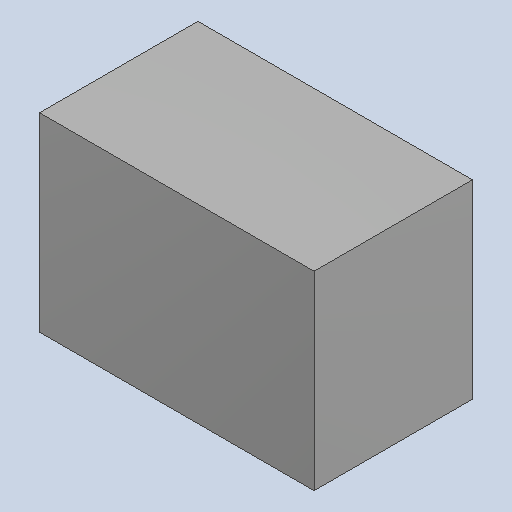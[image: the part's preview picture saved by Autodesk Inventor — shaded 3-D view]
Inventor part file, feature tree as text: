
AUTODESK INVENTOR PART (.ipt)
format: ipt  version: 2023.4 (Build 274418000, 418)  size: 82,432 bytes
history: native  units: mm
features: extrude x1
ambient origin geometry x8: Origin, YZ Plane, XZ Plane, XY Plane, X Axis, Y Axis, Z Axis, Center Point
bodies: Solid1 (feature_tree)
feature tree (1):
  extrude  "Extruded_1"  [1 undecoded]
note: 1 required parameter value undecoded (feature->parameter linkage not recoverable at this tier; creation-order binding heuristic only, values carry confidence <= 0.55)
